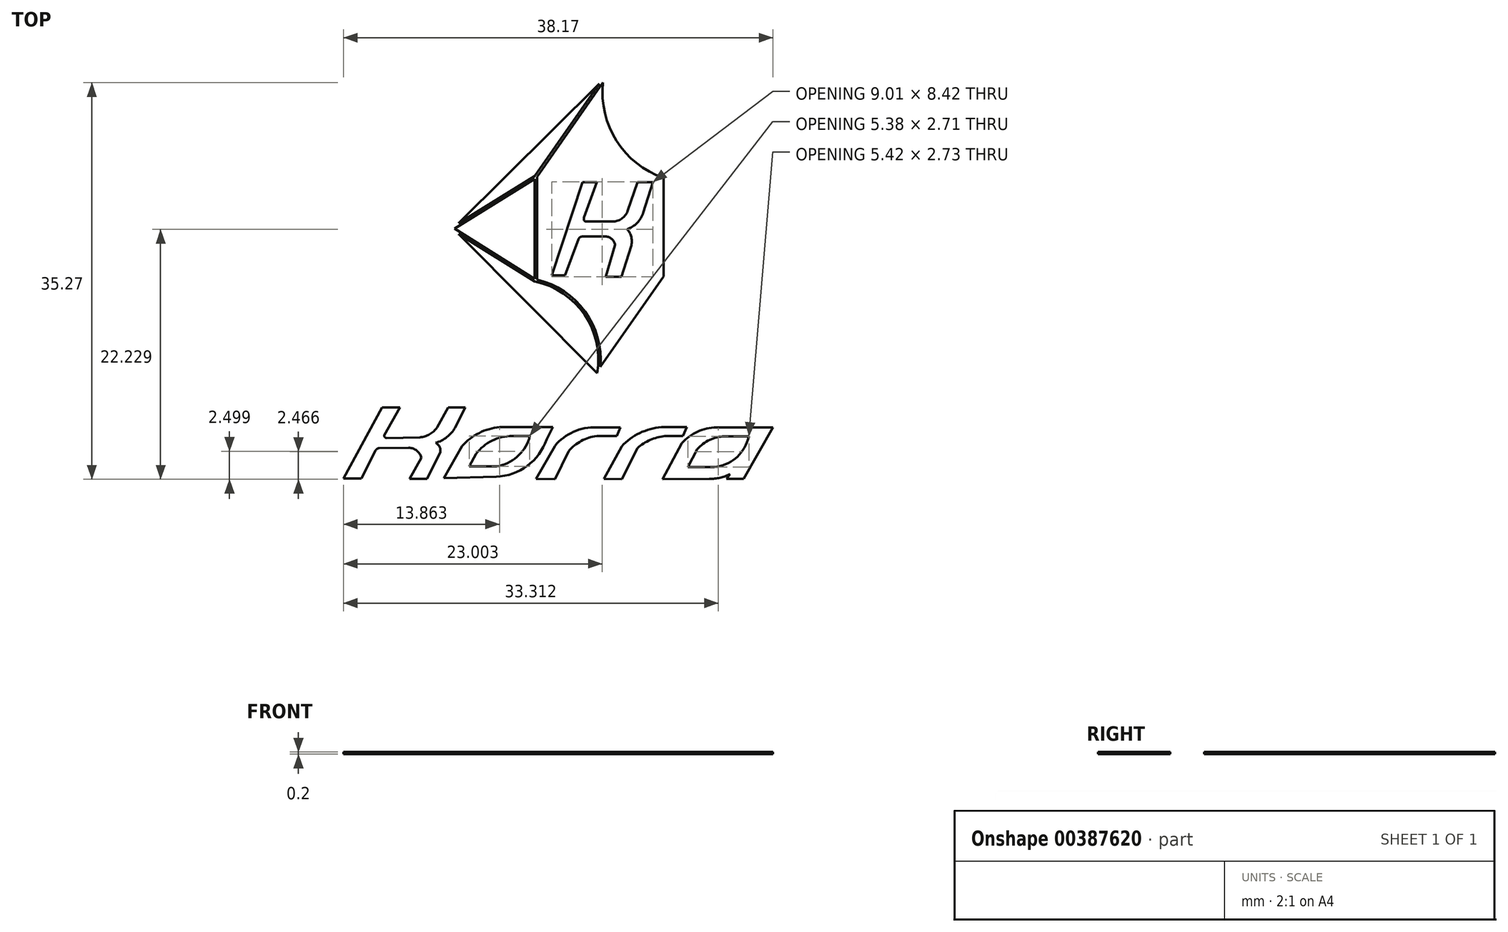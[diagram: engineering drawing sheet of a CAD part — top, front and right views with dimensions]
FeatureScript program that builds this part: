
annotation { "Feature Type Name" : "Feature", "Feature Type Description" : "" }
export const myFeature = defineFeature(function(context is Context, id is Id, definition is map)
    precondition{}
    {
        {
            var Q0;
            Q0=qCreatedBy(makeId("Top.planeOp"),FACE);
            var sketch = newSketch(context, id + "F0", { "sketchPlane" : qUnion([Q0])});
            skLineSegment(sketch, "E0", {"start": v(-5.5, 15.48) * mm, "end": v(-5.5, 6.6) * mm});
            skLineSegment(sketch, "E1", {"start": v(-5.5, 6.36) * mm, "end": v(-12.27, 10.6) * mm});
            skLineSegment(sketch, "E2", {"start": v(-5.5, 15.71) * mm, "end": v(-12.26, 11.53) * mm});
            skLineSegment(sketch, "E3", {"start": v(0.24, 23.94) * mm, "end": v(-5.5, 15.71) * mm});
            skLineSegment(sketch, "E4", {"start": v(0.88, 24.86) * mm, "end": v(-13.01, 11.06) * mm});
            skLineSegment(sketch, "E5", {"start": v(-13.01, 11.06) * mm, "end": v(0, -2.05) * mm});
            skLineSegment(sketch, "E6", {"start": v(0, -2.05) * mm, "end": v(6.14, 6.74) * mm});
            skLineSegment(sketch, "E7", {"start": v(6.14, 6.74) * mm, "end": v(6.14, 15.71) * mm});
            skArc(sketch, "E8", {"start": v(0.88, 24.86) * mm, "mid": v(1.76, 19.28) * mm, "end": v(6.14, 15.71) * mm});
            skArc(sketch, "E9", {"start": v(0.05, -1.81) * mm, "mid": v(-1.08, 3.4) * mm, "end": v(-5.5, 6.36) * mm});
            skLineSegment(sketch, "E10.0", {"start": v(5.94, 6.74) * mm, "end": v(5.94, 15.57) * mm});
            skArc(sketch, "E11.0", {"start": v(0.32, -1.24) * mm, "mid": v(-1.04, 3.7) * mm, "end": v(-5.3, 6.52) * mm});
            skLineSegment(sketch, "E12.0", {"start": v(-5.3, 15.65) * mm, "end": v(-5.3, 6.52) * mm});
            skLineSegment(sketch, "E13.0", {"start": v(0.55, 24.03) * mm, "end": v(-5.3, 15.65) * mm});
            skArc(sketch, "E14.trimOffspring", {"start": v(0.55, 24.03) * mm, "mid": v(1.77, 18.86) * mm, "end": v(5.94, 15.57) * mm});
            skLineSegment(sketch, "E15.trimOffspring", {"start": v(0.32, -1.24) * mm, "end": v(5.97, 6.85) * mm});
            skLineSegment(sketch, "E16.0", {"start": v(0.24, 23.94) * mm, "end": v(-12.26, 11.53) * mm});
            skLineSegment(sketch, "E17.0", {"start": v(-5.5, 15.48) * mm, "end": v(-12.64, 11.06) * mm});
            skLineSegment(sketch, "E18.0", {"start": v(-5.5, 6.6) * mm, "end": v(-12.64, 11.06) * mm});
            skLineSegment(sketch, "E19.trimOffspring", {"start": v(-12.27, 10.6) * mm, "end": v(0.05, -1.81) * mm});
            skLineSegment(sketch, "E20", {"start": v(-1.26, 15.2) * mm, "end": v(-4, 6.89) * mm});
            skLineSegment(sketch, "E21", {"start": v(-4, 6.89) * mm, "end": v(-2.81, 6.89) * mm});
            skLineSegment(sketch, "E22", {"start": v(-1.26, 15.2) * mm, "end": v(0, 15.2) * mm});
            skLineSegment(sketch, "E23", {"start": v(0, 15.2) * mm, "end": v(-1.26, 11.68) * mm});
            skLineSegment(sketch, "E24", {"start": v(-1.26, 11.68) * mm, "end": v(1.4, 11.68) * mm});
            skLineSegment(sketch, "E25", {"start": v(3.63, 15.18) * mm, "end": v(2.75, 12.6) * mm});
            skLineSegment(sketch, "E26", {"start": v(3.63, 15.18) * mm, "end": v(5.01, 15.18) * mm});
            skLineSegment(sketch, "E27", {"start": v(5.01, 15.18) * mm, "end": v(4.14, 12.47) * mm});
            skLineSegment(sketch, "E28", {"start": v(-2.81, 6.89) * mm, "end": v(-1.52, 10.35) * mm});
            skLineSegment(sketch, "E29", {"start": v(-1.52, 10.35) * mm, "end": v(0.78, 10.35) * mm});
            skLineSegment(sketch, "E30", {"start": v(1.64, 9.59) * mm, "end": v(0.82, 6.78) * mm});
            skLineSegment(sketch, "E31", {"start": v(0.82, 6.78) * mm, "end": v(2.2, 6.78) * mm});
            skLineSegment(sketch, "E32", {"start": v(2.2, 6.78) * mm, "end": v(3.05, 9.47) * mm});
            skArc(sketch, "E33", {"start": v(1.4, 11.68) * mm, "mid": v(2.22, 11.93) * mm, "end": v(2.75, 12.6) * mm});
            skArc(sketch, "E34", {"start": v(2.7, 11) * mm, "mid": v(3.6, 11.57) * mm, "end": v(4.14, 12.47) * mm});
            skArc(sketch, "E35", {"start": v(3.05, 9.47) * mm, "mid": v(3.09, 10.28) * mm, "end": v(2.7, 11) * mm});
            skArc(sketch, "E36", {"start": v(1.64, 9.59) * mm, "mid": v(1.36, 10.13) * mm, "end": v(0.78, 10.35) * mm});
            skArc(sketch, "E37", {"start": v(-1.13, 12.04) * mm, "mid": v(-1.13, 11.84) * mm, "end": v(-1.03, 11.68) * mm});
            skArc(sketch, "E38", {"start": v(-1.3, 10.35) * mm, "mid": v(-1.48, 10.29) * mm, "end": v(-1.6, 10.15) * mm});
            skArc(sketch, "E39", {"start": v(-15.71, -7.5) * mm, "mid": v(-14.84, -7.23) * mm, "end": v(-14.17, -6.61) * mm});
            skArc(sketch, "E40", {"start": v(-14.3, -8) * mm, "mid": v(-13.31, -7.49) * mm, "end": v(-12.58, -6.65) * mm});
            skArc(sketch, "E41", {"start": v(-13.9, -8.8) * mm, "mid": v(-13.97, -8.34) * mm, "end": v(-14.3, -8) * mm});
            skArc(sketch, "E42", {"start": v(-18.88, -7.32) * mm, "mid": v(-18.84, -7.48) * mm, "end": v(-18.7, -7.56) * mm});
            skArc(sketch, "E43", {"start": v(-19.32, -8.46) * mm, "mid": v(-19.54, -8.55) * mm, "end": v(-19.69, -8.73) * mm});
            skArc(sketch, "E44", {"start": v(-8.6, -6.6) * mm, "mid": v(-10.45, -7.12) * mm, "end": v(-11.96, -8.29) * mm});
            skArc(sketch, "E45", {"start": v(-8.87, -10.1) * mm, "mid": v(-7.09, -9.25) * mm, "end": v(-5.99, -7.62) * mm});
            skArc(sketch, "E46", {"start": v(0, -7.39) * mm, "mid": v(-1.37, -7.83) * mm, "end": v(-2.49, -8.74) * mm});
            skArc(sketch, "E47", {"start": v(0, -6.63) * mm, "mid": v(-2.05, -7.01) * mm, "end": v(-3.71, -8.27) * mm});
            skArc(sketch, "E48", {"start": v(5.75, -6.6) * mm, "mid": v(3.83, -7.13) * mm, "end": v(2.22, -8.31) * mm});
            skArc(sketch, "E49", {"start": v(6.05, -7.39) * mm, "mid": v(4.75, -7.75) * mm, "end": v(3.62, -8.46) * mm});
            skArc(sketch, "E50", {"start": v(10.64, -6.63) * mm, "mid": v(8.96, -7) * mm, "end": v(7.57, -8.03) * mm});
            skArc(sketch, "E51", {"start": v(11.38, -7.4) * mm, "mid": v(10.04, -7.74) * mm, "end": v(8.95, -8.57) * mm});
            skArc(sketch, "E52", {"start": v(10.45, -10.14) * mm, "mid": v(12.32, -9.38) * mm, "end": v(13.44, -7.7) * mm});
            skArc(sketch, "E53", {"start": v(-8.92, -11) * mm, "mid": v(-6.17, -10.04) * mm, "end": v(-4.44, -7.7) * mm});
            skLineSegment(sketch, "E54", {"start": v(-8.6, -6.6) * mm, "end": v(-3.9, -6.6) * mm});
            skLineSegment(sketch, "E55", {"start": v(-3.9, -6.6) * mm, "end": v(-4.44, -7.7) * mm});
            skLineSegment(sketch, "E56", {"start": v(-8.92, -11) * mm, "end": v(-13.57, -11.15) * mm});
            skLineSegment(sketch, "E57", {"start": v(-13.57, -11.15) * mm, "end": v(-11.96, -8.29) * mm});
            skLineSegment(sketch, "E58", {"start": v(-7.5, -7.39) * mm, "end": v(-5.95, -7.39) * mm});
            skLineSegment(sketch, "E59", {"start": v(-5.95, -7.39) * mm, "end": v(-5.99, -7.62) * mm});
            skLineSegment(sketch, "E60", {"start": v(-8.87, -10.1) * mm, "end": v(-11.33, -10.1) * mm});
            skLineSegment(sketch, "E61", {"start": v(-11.33, -10.1) * mm, "end": v(-10.72, -8.97) * mm});
            skArc(sketch, "E62", {"start": v(-7.5, -7.39) * mm, "mid": v(-9.29, -7.8) * mm, "end": v(-10.72, -8.97) * mm});
            skLineSegment(sketch, "E63", {"start": v(-19.07, -4.84) * mm, "end": v(-22.5, -11.18) * mm});
            skLineSegment(sketch, "E64", {"start": v(-22.5, -11.18) * mm, "end": v(-20.9, -11.18) * mm});
            skLineSegment(sketch, "E65", {"start": v(-20.9, -11.18) * mm, "end": v(-19.69, -8.73) * mm});
            skLineSegment(sketch, "E66", {"start": v(-19.32, -8.46) * mm, "end": v(-16.7, -8.44) * mm});
            skLineSegment(sketch, "E67", {"start": v(-16.62, -11.21) * mm, "end": v(-15.58, -9.33) * mm});
            skArc(sketch, "E68", {"start": v(-15.58, -9.33) * mm, "mid": v(-15.99, -8.69) * mm, "end": v(-16.7, -8.44) * mm});
            skLineSegment(sketch, "E69", {"start": v(-16.62, -11.21) * mm, "end": v(-15.07, -11.21) * mm});
            skLineSegment(sketch, "E70", {"start": v(-15.07, -11.21) * mm, "end": v(-13.9, -8.8) * mm});
            skLineSegment(sketch, "E71", {"start": v(-19.07, -4.84) * mm, "end": v(-17.47, -4.84) * mm});
            skLineSegment(sketch, "E72", {"start": v(-17.47, -4.84) * mm, "end": v(-18.88, -7.32) * mm});
            skLineSegment(sketch, "E73", {"start": v(-18.7, -7.56) * mm, "end": v(-15.71, -7.5) * mm});
            skLineSegment(sketch, "E74", {"start": v(-14.17, -6.61) * mm, "end": v(-13.21, -4.84) * mm});
            skLineSegment(sketch, "E75", {"start": v(-13.21, -4.84) * mm, "end": v(-11.68, -4.84) * mm});
            skLineSegment(sketch, "E76", {"start": v(-11.68, -4.84) * mm, "end": v(-12.58, -6.65) * mm});
            skLineSegment(sketch, "E77", {"start": v(-3.71, -8.27) * mm, "end": v(-5.37, -11.21) * mm});
            skLineSegment(sketch, "E78", {"start": v(-5.37, -11.21) * mm, "end": v(-3.71, -11.24) * mm});
            skLineSegment(sketch, "E79", {"start": v(-3.71, -11.24) * mm, "end": v(-2.49, -8.74) * mm});
            skLineSegment(sketch, "E80", {"start": v(0, -6.63) * mm, "end": v(2.12, -6.61) * mm});
            skLineSegment(sketch, "E81", {"start": v(2.12, -6.61) * mm, "end": v(1.79, -7.39) * mm});
            skLineSegment(sketch, "E82", {"start": v(1.79, -7.39) * mm, "end": v(0, -7.39) * mm});
            skLineSegment(sketch, "E83", {"start": v(2.22, -8.31) * mm, "end": v(0.66, -11.21) * mm});
            skLineSegment(sketch, "E84", {"start": v(0.66, -11.21) * mm, "end": v(2.22, -11.24) * mm});
            skLineSegment(sketch, "E85", {"start": v(2.22, -11.24) * mm, "end": v(3.62, -8.46) * mm});
            skLineSegment(sketch, "E86", {"start": v(5.75, -6.6) * mm, "end": v(8, -6.61) * mm});
            skLineSegment(sketch, "E87", {"start": v(8, -6.61) * mm, "end": v(7.66, -7.39) * mm});
            skLineSegment(sketch, "E88", {"start": v(7.66, -7.39) * mm, "end": v(6.05, -7.39) * mm});
            skLineSegment(sketch, "E89", {"start": v(7.57, -8.03) * mm, "end": v(5.84, -11.24) * mm});
            skLineSegment(sketch, "E90", {"start": v(5.84, -11.24) * mm, "end": v(10.03, -11.21) * mm});
            skLineSegment(sketch, "E91", {"start": v(10.64, -6.63) * mm, "end": v(15.67, -6.64) * mm});
            skLineSegment(sketch, "E92", {"start": v(15.67, -6.64) * mm, "end": v(13.07, -11.21) * mm});
            skLineSegment(sketch, "E93", {"start": v(13.07, -11.21) * mm, "end": v(11.54, -11.21) * mm});
            skLineSegment(sketch, "E94", {"start": v(11.54, -11.21) * mm, "end": v(11.86, -10.78) * mm});
            skArc(sketch, "E95", {"start": v(10.03, -11.21) * mm, "mid": v(10.97, -11.1) * mm, "end": v(11.86, -10.78) * mm});
            skLineSegment(sketch, "E96", {"start": v(11.38, -7.4) * mm, "end": v(13.52, -7.4) * mm});
            skLineSegment(sketch, "E97", {"start": v(13.52, -7.4) * mm, "end": v(13.44, -7.7) * mm});
            skLineSegment(sketch, "E98", {"start": v(10.45, -10.14) * mm, "end": v(8.1, -10.14) * mm});
            skLineSegment(sketch, "E99", {"start": v(8.1, -10.14) * mm, "end": v(8.95, -8.57) * mm});
            skSolve(sketch);
        }
        {
            var Q0;
            {var subQ8=sQuery(id+"F0.wireOp",EDGE,"E11.0");Q0=makeQuery(id+"F0.imprint","IMPRINT",FACE,{"disambiguationData":[TD([[makeQuery(id+"F0.imprint","IMPRINT",EDGE,{"derivedFrom":subQ8}),-1.0]])]});}
            var Q1;
            Q1=makeQuery(id+"F0.imprint","IMPRINT",FACE,{"disambiguationData":[TD([[makeQuery(id+"F0.imprint","IMPRINT",EDGE,{"derivedFrom":sQuery(id+"F0.wireOp",EDGE,"E1")}),1.0]])]});
            var Q2;
            Q2=makeQuery(id+"F0.imprint","IMPRINT",FACE,{"disambiguationData":[TD([[makeQuery(id+"F0.imprint","IMPRINT",EDGE,{"derivedFrom":sQuery(id+"F0.wireOp",EDGE,"E0")}),-1.0]])]});
            var Q3;
            Q3=makeQuery(id+"F0.imprint","IMPRINT",FACE,{"disambiguationData":[TD([[makeQuery(id+"F0.imprint","IMPRINT",EDGE,{"derivedFrom":sQuery(id+"F0.wireOp",EDGE,"E2")}),-1.0]])]});
            var Q4;
            Q4=makeQuery(id+"F0.imprint","IMPRINT",FACE,{"disambiguationData":[TD([[makeQuery(id+"F0.imprint","IMPRINT",EDGE,{"derivedFrom":sQuery(id+"F0.wireOp",EDGE,"E50")}),1.0]])]});
            var Q5;
            Q5=makeQuery(id+"F0.imprint","IMPRINT",FACE,{"disambiguationData":[TD([[makeQuery(id+"F0.imprint","IMPRINT",EDGE,{"derivedFrom":sQuery(id+"F0.wireOp",EDGE,"E48")}),1.0]])]});
            var Q6;
            Q6=makeQuery(id+"F0.imprint","IMPRINT",FACE,{"disambiguationData":[TD([[makeQuery(id+"F0.imprint","IMPRINT",EDGE,{"derivedFrom":sQuery(id+"F0.wireOp",EDGE,"E46")}),-1.0]])]});
            var Q7;
            Q7=makeQuery(id+"F0.imprint","IMPRINT",FACE,{"disambiguationData":[TD([[makeQuery(id+"F0.imprint","IMPRINT",EDGE,{"derivedFrom":sQuery(id+"F0.wireOp",EDGE,"E44")}),1.0]])]});
            var Q8;
            Q8=makeQuery(id+"F0.imprint","IMPRINT",FACE,{"disambiguationData":[TD([[makeQuery(id+"F0.imprint","IMPRINT",EDGE,{"derivedFrom":sQuery(id+"F0.wireOp",EDGE,"E39")}),-1.0]])]});
            extrude(context, id + "F1", {"entities" : qUnion([Q0, Q1, Q2, Q3, Q4, Q5, Q6, Q7, Q8]), "oppositeDirection" : true, "depth" : .2 * mm});
        }
        {
            var Q0;
            Q0=makeQuery(id+"F1.opExtrude","SWEPT_BODY",BODY,{"disambiguationData":[OSD([sQuery(id+"F0.wireOp",EDGE,"E1"),sQuery(id+"F0.wireOp",EDGE,"E9"),sQuery(id+"F0.wireOp",EDGE,"E19.trimOffspring")])]});
            var Q1;
            Q1=makeQuery(id+"F1.opExtrude","SWEPT_BODY",BODY,{"disambiguationData":[OSD([sQuery(id+"F0.wireOp",EDGE,"E39"),sQuery(id+"F0.wireOp",EDGE,"E40"),sQuery(id+"F0.wireOp",EDGE,"E41"),sQuery(id+"F0.wireOp",EDGE,"E42"),sQuery(id+"F0.wireOp",EDGE,"E43"),sQuery(id+"F0.wireOp",EDGE,"E63"),sQuery(id+"F0.wireOp",EDGE,"E64"),sQuery(id+"F0.wireOp",EDGE,"E65"),sQuery(id+"F0.wireOp",EDGE,"E66"),sQuery(id+"F0.wireOp",EDGE,"E67"),sQuery(id+"F0.wireOp",EDGE,"E68"),sQuery(id+"F0.wireOp",EDGE,"E69"),sQuery(id+"F0.wireOp",EDGE,"E70"),sQuery(id+"F0.wireOp",EDGE,"E71"),sQuery(id+"F0.wireOp",EDGE,"E72"),sQuery(id+"F0.wireOp",EDGE,"E73"),sQuery(id+"F0.wireOp",EDGE,"E74"),sQuery(id+"F0.wireOp",EDGE,"E75"),sQuery(id+"F0.wireOp",EDGE,"E76")])]});
            var Q2;
            Q2=makeQuery(id+"F1.opExtrude","SWEPT_BODY",BODY,{"disambiguationData":[OSD([sQuery(id+"F0.wireOp",EDGE,"E44"),sQuery(id+"F0.wireOp",EDGE,"E45"),sQuery(id+"F0.wireOp",EDGE,"E53"),sQuery(id+"F0.wireOp",EDGE,"E54"),sQuery(id+"F0.wireOp",EDGE,"E55"),sQuery(id+"F0.wireOp",EDGE,"E56"),sQuery(id+"F0.wireOp",EDGE,"E57"),sQuery(id+"F0.wireOp",EDGE,"E58"),sQuery(id+"F0.wireOp",EDGE,"E59"),sQuery(id+"F0.wireOp",EDGE,"E60"),sQuery(id+"F0.wireOp",EDGE,"E61"),sQuery(id+"F0.wireOp",EDGE,"E62")])]});
            var Q3;
            Q3=makeQuery(id+"F1.opExtrude","SWEPT_BODY",BODY,{"disambiguationData":[OSD([sQuery(id+"F0.wireOp",EDGE,"E46"),sQuery(id+"F0.wireOp",EDGE,"E47"),sQuery(id+"F0.wireOp",EDGE,"E77"),sQuery(id+"F0.wireOp",EDGE,"E78"),sQuery(id+"F0.wireOp",EDGE,"E79"),sQuery(id+"F0.wireOp",EDGE,"E80"),sQuery(id+"F0.wireOp",EDGE,"E81"),sQuery(id+"F0.wireOp",EDGE,"E82")])]});
            var Q4;
            Q4=makeQuery(id+"F1.opExtrude","SWEPT_BODY",BODY,{"disambiguationData":[OSD([sQuery(id+"F0.wireOp",EDGE,"E0"),sQuery(id+"F0.wireOp",EDGE,"E17.0"),sQuery(id+"F0.wireOp",EDGE,"E18.0")])]});
            var Q5;
            Q5=makeQuery(id+"F1.opExtrude","SWEPT_BODY",BODY,{"disambiguationData":[OSD([sQuery(id+"F0.wireOp",EDGE,"E2"),sQuery(id+"F0.wireOp",EDGE,"E3"),sQuery(id+"F0.wireOp",EDGE,"E16.0")])]});
            var Q6;
            Q6=makeQuery(id+"F1.opExtrude","SWEPT_BODY",BODY,{"disambiguationData":[OSD([sQuery(id+"F0.wireOp",EDGE,"E10.0"),sQuery(id+"F0.wireOp",EDGE,"E11.0"),sQuery(id+"F0.wireOp",EDGE,"E12.0"),sQuery(id+"F0.wireOp",EDGE,"E13.0"),sQuery(id+"F0.wireOp",EDGE,"E14.trimOffspring"),sQuery(id+"F0.wireOp",EDGE,"E15.trimOffspring"),sQuery(id+"F0.wireOp",EDGE,"E20"),sQuery(id+"F0.wireOp",EDGE,"E21"),sQuery(id+"F0.wireOp",EDGE,"E22"),sQuery(id+"F0.wireOp",EDGE,"E23"),sQuery(id+"F0.wireOp",EDGE,"E24"),sQuery(id+"F0.wireOp",EDGE,"E25"),sQuery(id+"F0.wireOp",EDGE,"E26"),sQuery(id+"F0.wireOp",EDGE,"E27"),sQuery(id+"F0.wireOp",EDGE,"E28"),sQuery(id+"F0.wireOp",EDGE,"E29"),sQuery(id+"F0.wireOp",EDGE,"E30"),sQuery(id+"F0.wireOp",EDGE,"E31"),sQuery(id+"F0.wireOp",EDGE,"E32"),sQuery(id+"F0.wireOp",EDGE,"E33"),sQuery(id+"F0.wireOp",EDGE,"E34"),sQuery(id+"F0.wireOp",EDGE,"E35"),sQuery(id+"F0.wireOp",EDGE,"E36"),sQuery(id+"F0.wireOp",EDGE,"E37"),sQuery(id+"F0.wireOp",EDGE,"E38")])]});
            var Q7;
            Q7=makeQuery(id+"F1.opExtrude","SWEPT_BODY",BODY,{"disambiguationData":[OSD([sQuery(id+"F0.wireOp",EDGE,"E48"),sQuery(id+"F0.wireOp",EDGE,"E49"),sQuery(id+"F0.wireOp",EDGE,"E83"),sQuery(id+"F0.wireOp",EDGE,"E84"),sQuery(id+"F0.wireOp",EDGE,"E85"),sQuery(id+"F0.wireOp",EDGE,"E86"),sQuery(id+"F0.wireOp",EDGE,"E87"),sQuery(id+"F0.wireOp",EDGE,"E88")])]});
            var Q8;
            Q8=makeQuery(id+"F1.opExtrude","SWEPT_BODY",BODY,{"disambiguationData":[OSD([sQuery(id+"F0.wireOp",EDGE,"E50"),sQuery(id+"F0.wireOp",EDGE,"E51"),sQuery(id+"F0.wireOp",EDGE,"E52"),sQuery(id+"F0.wireOp",EDGE,"E89"),sQuery(id+"F0.wireOp",EDGE,"E90"),sQuery(id+"F0.wireOp",EDGE,"E91"),sQuery(id+"F0.wireOp",EDGE,"E92"),sQuery(id+"F0.wireOp",EDGE,"E93"),sQuery(id+"F0.wireOp",EDGE,"E94"),sQuery(id+"F0.wireOp",EDGE,"E95"),sQuery(id+"F0.wireOp",EDGE,"E96"),sQuery(id+"F0.wireOp",EDGE,"E97"),sQuery(id+"F0.wireOp",EDGE,"E98"),sQuery(id+"F0.wireOp",EDGE,"E99")])]});
            var Q9;
            Q9=qCreatedBy(makeId("Origin.pointOp"),VERTEX);
            transform(context, id + "F2", {"entities" : qUnion([Q0, Q1, Q2, Q3, Q4, Q5, Q6, Q7, Q8]), "transformType" : TransformType.SCALE_UNIFORMLY, "scale" : 1, "scalePoint" : qUnion([Q9]), "makeCopy" : false});
        }
    });
